# Revit family: TemID_IP вызывная панель с распознаванием лиц и Mifare VEX-B21A MF BLE
name_source: partatom
category: Охранная сигнализация
units: mm (PartAtom-declared; Revit-internal decimal feet)

## family parameters
Всегда вертикально = Нет
На основе рабочей плоскости = Нет
Общий = Да
При загрузке вырезать с полостями = Нет
Размер круглого соединителя = Использовать диаметр
Сохранять ориентацию аннотаций = Нет
Тип детали = Нормальный
Точка расчета площади = Да

## types (3) — shared parameters
=Габариты= = =Габариты=
ADSK_Единица измерения = шт.
ADSK_Завод-изготовитель = TemID
ADSK_Количество = 1
ADSK_Наименование = IP вызывная панель с распознаванием лиц
ADSK_Обозначение = RD
ADSK_Раздел спецификации = 3. Периферийное оборудование
ADSK_Размер_Высота = 380 мм
ADSK_Размер_Глубина = 56 мм
ADSK_Размер_Ширина = 158 мм
URL = https://temid-global.ru
Зона обслуживания_Отступ от прибора = 50 мм
Материал_Корпус = Светло-серый
УГО_Тип = УГО_СКУД_Панель_вызова_видеодомофона
zero-valued in all types: Отметка по умолчанию

## per-type parameters (varying)
| type | ADSK_Марка | ADSK_Тип |
| Mifare VEX-B21A | Mifare VEX-B21A | Mifare VEX-B21A |
| Mifare VEX-B21A MF | Mifare VEX-B21A MF | Mifare VEX-B21A MF |
| Mifare VEX-B21A MF BLE | Mifare VEX-B21A mf ble | Mifare VEX-B21A mf ble |
